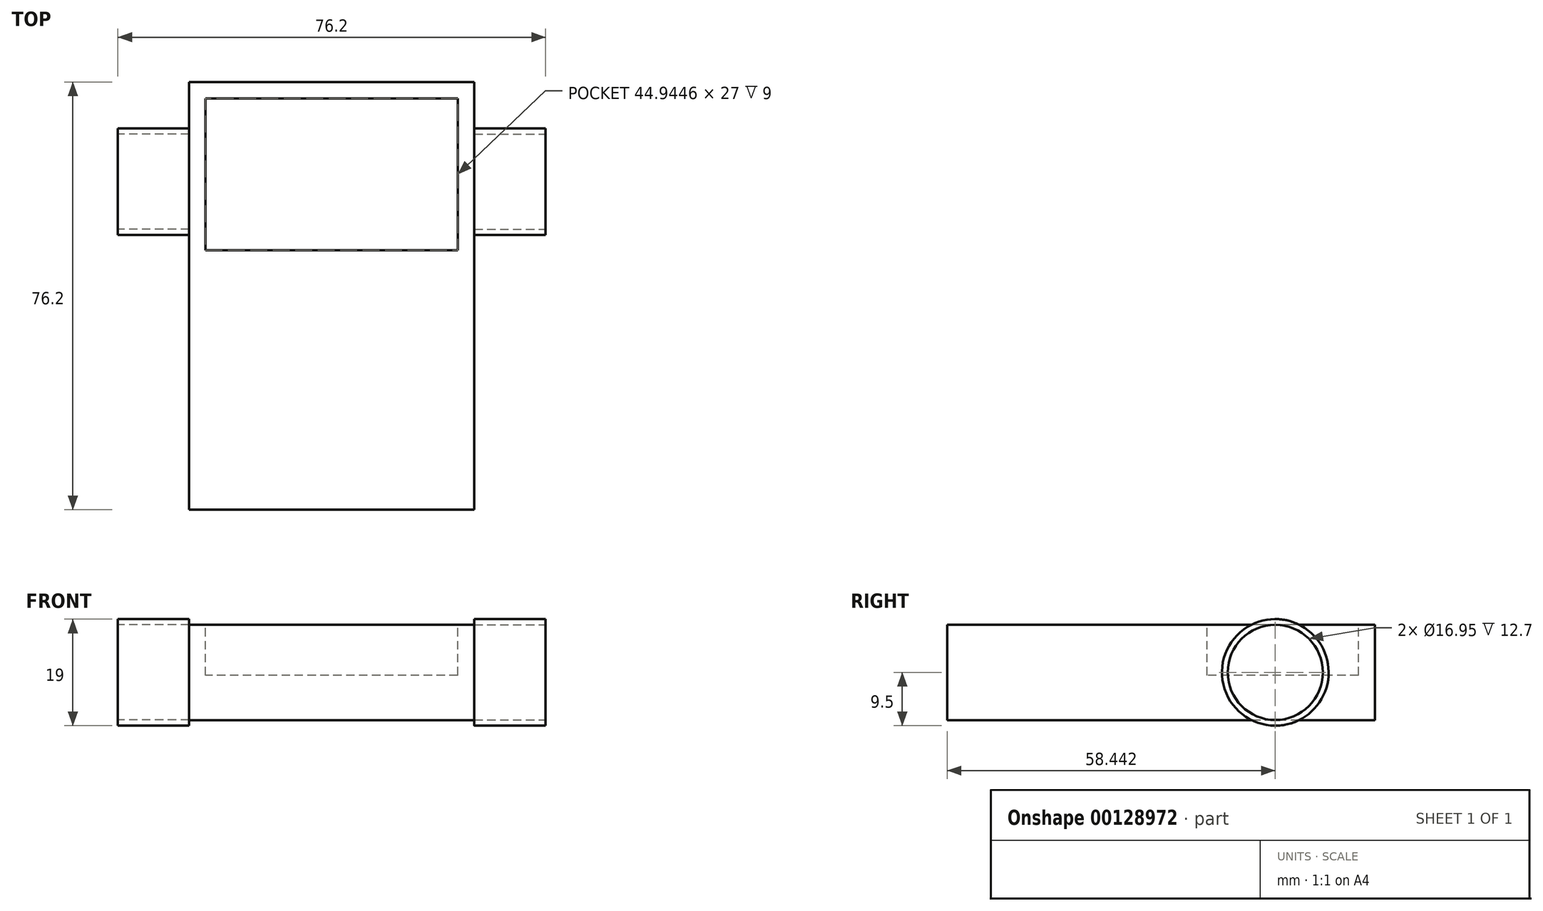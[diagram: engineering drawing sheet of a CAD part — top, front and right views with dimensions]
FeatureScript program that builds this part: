
annotation { "Feature Type Name" : "Feature", "Feature Type Description" : "" }
export const myFeature = defineFeature(function(context is Context, id is Id, definition is map)
    precondition{}
    {
        {
            var Q0;
            Q0=qCreatedBy(makeId("Top.planeOp"),FACE);
            var sketch = newSketch(context, id + "F0", { "sketchPlane" : qUnion([Q0])});
            skLineSegment(sketch, "E0.bottom", {"start": v(25.4, 38.1) * mm, "end": v(-25.4, 38.1) * mm});
            skLineSegment(sketch, "E0.top", {"start": v(25.4, -38.1) * mm, "end": v(-25.4, -38.1) * mm});
            skLineSegment(sketch, "E0.left", {"start": v(25.4, 38.1) * mm, "end": v(25.4, -38.1) * mm});
            skLineSegment(sketch, "E0.right", {"start": v(-25.4, 38.1) * mm, "end": v(-25.4, -38.1) * mm});
            skPoint(sketch, "E0.middle", {"position": v(0, 0) * mm});
            skSolve(sketch);
        }
        {
            var Q0;
            Q0 = qSketchRegion(id + "F0", true);
            extrude(context, id + "F1", {"entities" : qUnion([Q0]), "depth" : 17 * mm});
        }
        {
            var Q0;
            Q0=makeQuery(id+"F1.opExtrude","CAP_FACE",FACE,{"disambiguationData":[OSD([sQuery(id+"F0.wireOp",EDGE,"E0.bottom"),sQuery(id+"F0.wireOp",EDGE,"E0.top"),sQuery(id+"F0.wireOp",EDGE,"E0.left"),sQuery(id+"F0.wireOp",EDGE,"E0.right")])],"isStart":false});
            var sketch = newSketch(context, id + "F2", { "sketchPlane" : qUnion([Q0])});
            skLineSegment(sketch, "E1", {"start": v(22.47, 35.16) * mm, "end": v(-22.47, 35.16) * mm, "construction": true});
            skLineSegment(sketch, "E2", {"start": v(-22.47, 35.16) * mm, "end": v(-22.47, -34.58) * mm, "construction": true});
            skLineSegment(sketch, "E3", {"start": v(-22.47, -34.58) * mm, "end": v(22.47, -34.58) * mm, "construction": true});
            skLineSegment(sketch, "E4", {"start": v(22.47, -34.58) * mm, "end": v(22.47, 35.16) * mm, "construction": true});
            skSolve(sketch);
        }
        {
            var Q0;
            Q0=makeQuery(id+"F2.imprint","IMPRINT",FACE,{"disambiguationData":[TD([[makeQuery(id+"F2.imprint","IMPRINT",EDGE,{"derivedFrom":makeQuery(id+"F1.opExtrude","CAP_EDGE",EDGE,{"disambiguationData":[OSD([sQuery(id+"F0.wireOp",EDGE,"E0.bottom")])],"isStart":false})}),1.0]])]});
            var sketch = newSketch(context, id + "F3", { "sketchPlane" : qUnion([Q0])});
            skLineSegment(sketch, "E5.bottom", {"start": v(22.47, 35.16) * mm, "end": v(-22.47, 35.16) * mm});
            skLineSegment(sketch, "E5.top", {"start": v(22.47, 8.16) * mm, "end": v(-22.47, 8.16) * mm});
            skLineSegment(sketch, "E5.left", {"start": v(22.47, 35.16) * mm, "end": v(22.47, 8.16) * mm});
            skLineSegment(sketch, "E5.right", {"start": v(-22.47, 35.16) * mm, "end": v(-22.47, 8.16) * mm});
            skSolve(sketch);
        }
        {
            var Q0;
            Q0 = qSketchRegion(id + "F3", true);
            extrude(context, id + "F4", {"entities" : qUnion([Q0]), "operationType" : NewBodyOperationType.REMOVE, "oppositeDirection" : true, "depth" : 9 * mm});
        }
        {
            var Q0;
            Q0=makeQuery(id+"F1.opExtrude","SWEPT_FACE",FACE,{"disambiguationData":[OSD([sQuery(id+"F0.wireOp",EDGE,"E0.left")])]});
            var sketch = newSketch(context, id + "F5", { "sketchPlane" : qUnion([Q0])});
            skCircle(sketch, "E6", {"center": v(20.34, 8.5) * mm, "radius": 9.5 * mm});
            skPoint(sketch, "E6.centerSnap0", {"position": v(38.1, 8.5) * mm});
            skSolve(sketch);
        }
        {
            var Q0;
            Q0 = qSketchRegion(id + "F5", true);
            extrude(context, id + "F6", {"entities" : qUnion([Q0]), "operationType" : NewBodyOperationType.ADD, "depth" : 12.7 * mm});
        }
        {
            var Q0;
            Q0=makeQuery(id+"F6.opExtrude","CAP_FACE",FACE,{"disambiguationData":[OSD([sQuery(id+"F5.wireOp",EDGE,"E6")])],"isStart":false});
            var sketch = newSketch(context, id + "F7", { "sketchPlane" : qUnion([Q0])});
            skCircle(sketch, "E7", {"center": v(20.34, 8.5) * mm, "radius": 8.48 * mm});
            skCircle(sketch, "E8", {"center": v(20.34, 8.5) * mm, "radius": 8.47 * mm});
            skSolve(sketch);
        }
        {
            var Q0;
            Q0 = qSketchRegion(id + "F7", true);
            extrude(context, id + "F8", {"entities" : qUnion([Q0]), "operationType" : NewBodyOperationType.REMOVE, "oppositeDirection" : true, "depth" : 12.7 * mm});
        }
        {
            var Q0;
            Q0=makeQuery(id+"F1.opExtrude","SWEPT_FACE",FACE,{"disambiguationData":[OSD([sQuery(id+"F0.wireOp",EDGE,"E0.right")])]});
            var sketch = newSketch(context, id + "F9", { "sketchPlane" : qUnion([Q0])});
            skCircle(sketch, "E9", {"center": v(-20.34, 8.5) * mm, "radius": 9.5 * mm});
            skSolve(sketch);
        }
        {
            var Q0;
            Q0 = qSketchRegion(id + "F9", true);
            extrude(context, id + "F10", {"entities" : qUnion([Q0]), "operationType" : NewBodyOperationType.ADD, "depth" : 12.7 * mm});
        }
        {
            var Q0;
            Q0=makeQuery(id+"F10.opExtrude","CAP_FACE",FACE,{"disambiguationData":[OSD([sQuery(id+"F9.wireOp",EDGE,"E9")])],"isStart":false});
            var sketch = newSketch(context, id + "F11", { "sketchPlane" : qUnion([Q0])});
            skCircle(sketch, "E10", {"center": v(-20.34, 8.5) * mm, "radius": 8.47 * mm});
            skSolve(sketch);
        }
        {
            var Q0;
            Q0 = qSketchRegion(id + "F11", true);
            extrude(context, id + "F12", {"entities" : qUnion([Q0]), "operationType" : NewBodyOperationType.REMOVE, "oppositeDirection" : true, "depth" : 12.7 * mm});
        }
    });
